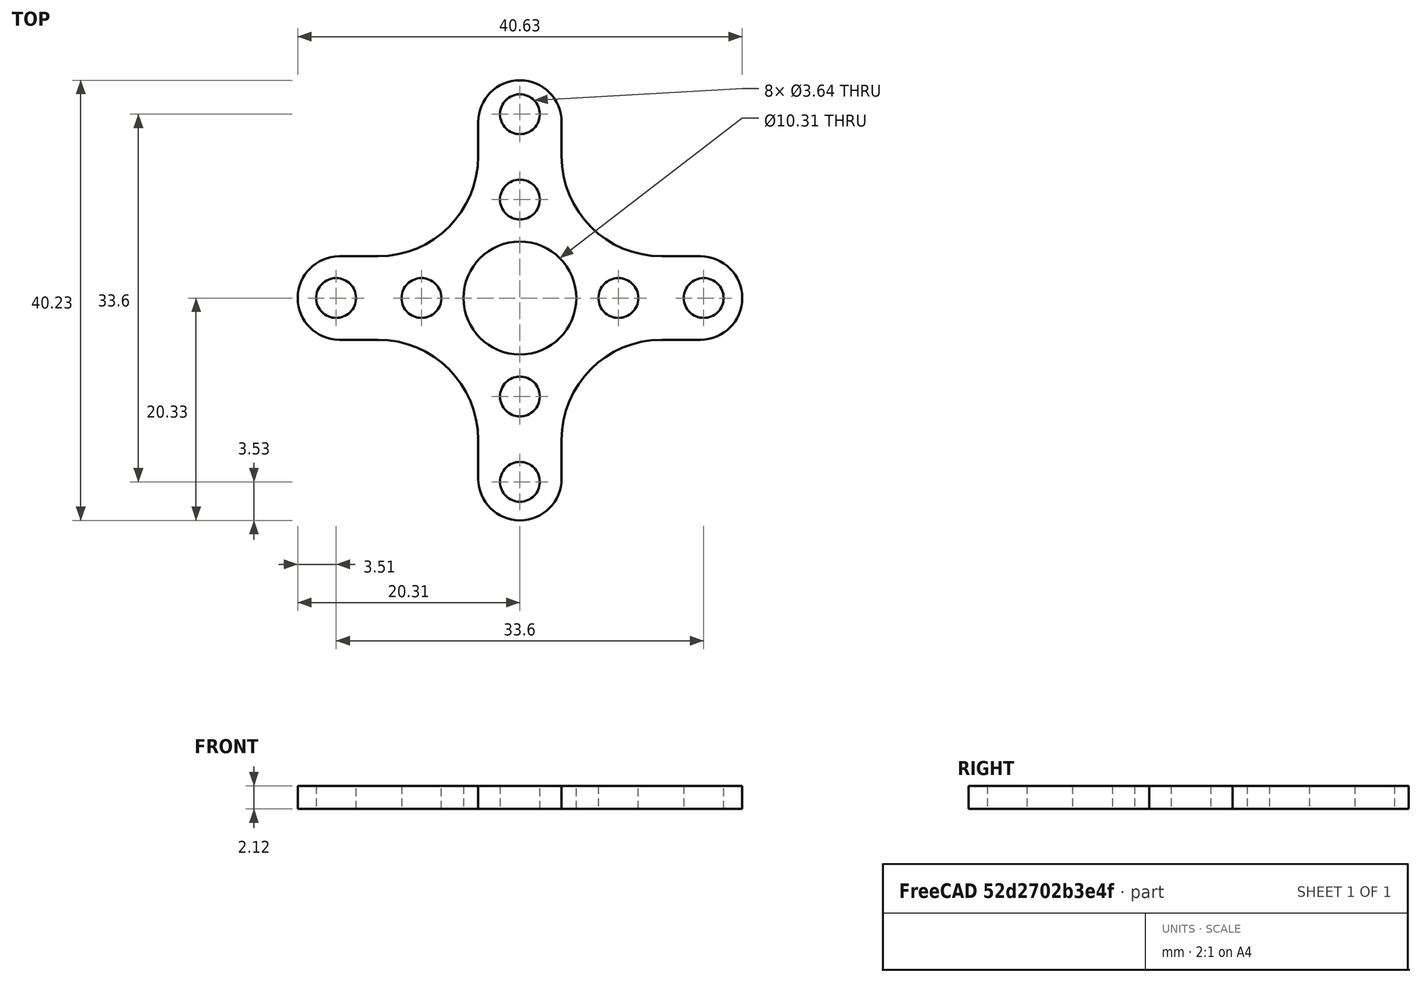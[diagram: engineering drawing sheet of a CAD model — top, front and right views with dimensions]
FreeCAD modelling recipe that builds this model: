
FCSTD DOCUMENT  (FreeCAD 0.19R22198 (Git))
Label: Brushless_Motor_Mount
License: All rights reserved
LicenseURL: http://en.wikipedia.org/wiki/All_rights_reserved
objects: Mesh::Feature×1, Sketcher::SketchObject×1, PartDesign::Pad×1, PartDesign::Body×1
note: 4 computed .brp shape members not serialized (recipe doc carries the construction recipe); baked Part::Feature solids carry a one-line shape summary decoded from their .brp

FEATURE [Mesh::Feature] Brushless_Motor_A2212_13T_1000KV
  Placement = pos=(0,0,21) rot=(0,0,1;0rad)
FEATURE [Sketcher::SketchObject] Sketch
  MapMode = 5
  Support = -> [XY_Plane]
  sketch-geometry (33):
    g0: LineSegment [constr] StartX=-20.325 StartY=3.815 StartZ=0 EndX=20.325 EndY=3.815 EndZ=0
    g1: LineSegment [constr] StartX=20.325 StartY=3.815 StartZ=0 EndX=20.325 EndY=-3.815 EndZ=0
    g2: LineSegment [constr] StartX=20.325 StartY=-3.815 StartZ=0 EndX=-20.325 EndY=-3.815 EndZ=0
    g3: LineSegment [constr] StartX=-20.325 StartY=-3.815 StartZ=0 EndX=-20.325 EndY=3.815 EndZ=0
    g4: LineSegment [constr] StartX=-3.815 StartY=20.325 StartZ=0 EndX=3.815 EndY=20.325 EndZ=0
    g5: LineSegment [constr] StartX=3.815 StartY=20.325 StartZ=0 EndX=3.815 EndY=-20.325 EndZ=0
    g6: LineSegment [constr] StartX=3.815 StartY=-20.325 StartZ=0 EndX=-3.815 EndY=-20.325 EndZ=0
    g7: LineSegment [constr] StartX=-3.815 StartY=-20.325 StartZ=0 EndX=-3.815 EndY=20.325 EndZ=0
    g8: ArcOfCircle CenterX=-16.4978 CenterY=0 CenterZ=0 NormalX=0 NormalY=0 NormalZ=1 AngleXU=0 Radius=3.815 StartAngle=1.5708 EndAngle=4.71239
    g9: LineSegment StartX=-16.4978 StartY=3.815 StartZ=0 EndX=-12.965 EndY=3.815 EndZ=0
    g10: LineSegment StartX=-16.4978 StartY=-3.815 StartZ=0 EndX=-12.965 EndY=-3.815 EndZ=0
    g11: ArcOfCircle CenterX=0 CenterY=16.0828 CenterZ=0 NormalX=0 NormalY=0 NormalZ=1 AngleXU=0 Radius=3.815 StartAngle=6.28319 EndAngle=9.42478
    g12: LineSegment StartX=-3.815 StartY=12.965 StartZ=0 EndX=-3.815 EndY=16.0828 EndZ=0
    g13: ArcOfCircle CenterX=16.504 CenterY=0 CenterZ=0 NormalX=0 NormalY=0 NormalZ=1 AngleXU=0 Radius=3.815 StartAngle=4.71239 EndAngle=7.85398
    g14: LineSegment StartX=3.815 StartY=16.0828 StartZ=0 EndX=3.815 EndY=12.965 EndZ=0
    g15: LineSegment StartX=12.965 StartY=3.815 StartZ=0 EndX=16.504 EndY=3.815 EndZ=0
    g16: ArcOfCircle CenterX=0 CenterY=-16.5107 CenterZ=0 NormalX=0 NormalY=0 NormalZ=1 AngleXU=0 Radius=3.815 StartAngle=3.14159 EndAngle=6.28319
    g17: LineSegment StartX=-3.815 StartY=-12.965 StartZ=0 EndX=-3.815 EndY=-16.5107 EndZ=0
    g18: LineSegment StartX=3.815 StartY=-16.5107 StartZ=0 EndX=3.815 EndY=-12.965 EndZ=0
    g19: LineSegment StartX=16.504 StartY=-3.815 StartZ=0 EndX=12.965 EndY=-3.815 EndZ=0
    g20: Circle CenterX=0 CenterY=0 CenterZ=0 NormalX=0 NormalY=0 NormalZ=1 AngleXU=0 Radius=5.155
    g21: ArcOfCircle CenterX=-12.965 CenterY=12.965 CenterZ=0 NormalX=0 NormalY=0 NormalZ=1 AngleXU=0 Radius=9.15 StartAngle=4.71239 EndAngle=6.28319
    g22: ArcOfCircle CenterX=12.965 CenterY=12.965 CenterZ=0 NormalX=0 NormalY=0 NormalZ=1 AngleXU=0 Radius=9.15 StartAngle=3.14159 EndAngle=4.71239
    g23: ArcOfCircle CenterX=12.965 CenterY=-12.965 CenterZ=0 NormalX=0 NormalY=0 NormalZ=1 AngleXU=0 Radius=9.15 StartAngle=1.5708 EndAngle=3.14159
    g24: ArcOfCircle CenterX=-12.965 CenterY=-12.965 CenterZ=0 NormalX=0 NormalY=0 NormalZ=1 AngleXU=0 Radius=9.15 StartAngle=0 EndAngle=1.5708
    g25: Circle CenterX=16.8 CenterY=0 CenterZ=0 NormalX=0 NormalY=0 NormalZ=1 AngleXU=0 Radius=1.82
    g26: Circle CenterX=0 CenterY=-16.8 CenterZ=0 NormalX=0 NormalY=0 NormalZ=1 AngleXU=0 Radius=1.82
    g27: Circle CenterX=0 CenterY=16.8 CenterZ=0 NormalX=0 NormalY=0 NormalZ=1 AngleXU=0 Radius=1.82
    g28: Circle CenterX=-16.8 CenterY=0 CenterZ=0 NormalX=0 NormalY=0 NormalZ=1 AngleXU=0 Radius=1.82
    g29: Circle CenterX=-9 CenterY=0 CenterZ=0 NormalX=0 NormalY=0 NormalZ=1 AngleXU=0 Radius=1.82
    g30: Circle CenterX=0 CenterY=9 CenterZ=0 NormalX=0 NormalY=0 NormalZ=1 AngleXU=0 Radius=1.82
    g31: Circle CenterX=9 CenterY=0 CenterZ=0 NormalX=0 NormalY=0 NormalZ=1 AngleXU=0 Radius=1.82
    g32: Circle CenterX=0 CenterY=-9 CenterZ=0 NormalX=0 NormalY=0 NormalZ=1 AngleXU=0 Radius=1.82
  constraints (89):
    c: Coincident(g0,g1)
    c: Coincident(g1,g2)
    c: Coincident(g2,g3)
    c: Coincident(g3,g0)
    c: Horizontal(g0)
    c: Horizontal(g2)
    c: Vertical(g1)
    c: Vertical(g3)
    c: Distance(g0) = 40.65
    c: Distance(g3) = 7.63
    c: Distance(g-1,g0) = 3.815
    c: Distance(g-1,g3) = 20.325
    c: Coincident(g4,g5)
    c: Coincident(g5,g6)
    c: Coincident(g6,g7)
    c: Coincident(g7,g4)
    c: Horizontal(g4)
    c: Horizontal(g6)
    c: Vertical(g5)
    c: Vertical(g7)
    c: Distance(g6) = 7.63
    c: Distance(g5) = 40.65
    c: Distance(g-1,g5) = 3.815
    c: Distance(g-1,g4) = 20.325
    c: PointOnObject(g8,g-1)
    c: PointOnObject(g8,g0)
    c: PointOnObject(g8,g2)
    c: Radius(g8) = 3.815
    c: Coincident(g9,g8)
    c: Horizontal(g9)
    c: Coincident(g10,g8)
    c: PointOnObject(g11,g-2)
    c: PointOnObject(g11,g7)
    c: Radius(g11) = 3.815
    c: Coincident(g12,g11)
    c: PointOnObject(g13,g-1)
    c: PointOnObject(g13,g0)
    c: PointOnObject(g13,g2)
    c: Radius(g13) = 3.815
    c: Coincident(g14,g11)
    c: Vertical(g14)
    c: Coincident(g15,g13)
    c: Horizontal(g15)
    c: PointOnObject(g16,g-2)
    c: PointOnObject(g16,g5)
    c: PointOnObject(g16,g7)
    c: Radius(g16) = 3.815
    c: Coincident(g17,g16)
    c: Vertical(g17)
    c: Coincident(g18,g16)
    c: Coincident(g19,g13)
    c: Horizontal(g19)
    c: Coincident(g20,g-1)
    c: Radius(g20) = 5.155
    c: Tangent(g9,g21) = -1.5708
    c: Tangent(g12,g21) = -1.5708
    c: Radius(g21) = 9.15
    c: PointOnObject(g12,g7)
    c: Tangent(g14,g22) = -1.5708
    c: Tangent(g15,g22) = -1.5708
    c: PointOnObject(g14,g5)
    c: Radius(g22) = 9.15
    c: Tangent(g19,g23) = -1.5708
    c: Coincident(g18,g23)
    c: PointOnObject(g18,g5)
    c: Radius(g23) = 9.15
    c: Tangent(g10,g24) = 1.5708
    c: Tangent(g17,g24) = 1.5708
    c: PointOnObject(g10,g2)
    c: Radius(g24) = 9.15
    c: PointOnObject(g25,g-1)
    c: Radius(g25) = 1.82
    c: DistanceX(g-2,g25) = 16.8
    c: Equal(g25,g26) = 1.82
    c: PointOnObject(g26,g-2)
    c: Equal(g25,g27) = 1.82
    c: PointOnObject(g27,g-2)
    c: PointOnObject(g28,g-1)
    c: DistanceX(g-2,g28) = -16.8
    c: DistanceY(g-1,g26) = -16.8
    c: DistanceY(g-1,g27) = 16.8
    c: PointOnObject(g29,g-1)
    c: PointOnObject(g30,g-2)
    c: PointOnObject(g31,g-1)
    c: PointOnObject(g32,g-2)
    c: DistanceY(g-1,g32) = -9
    c: DistanceY(g-1,g30) = 9
    c: DistanceX(g-2,g31) = 9
    c: DistanceX(g-2,g29) = -9
FEATURE [PartDesign::Pad] Pad
  Length = 2.12
  Length2 = 100
  Profile = -> Sketch
  Type = 0
FEATURE [PartDesign::Body] Body  label="BrushlessMotorMount"
  Group = -> [Sketch,Pad]
  Origin = -> Origin
  Tip = -> Pad
